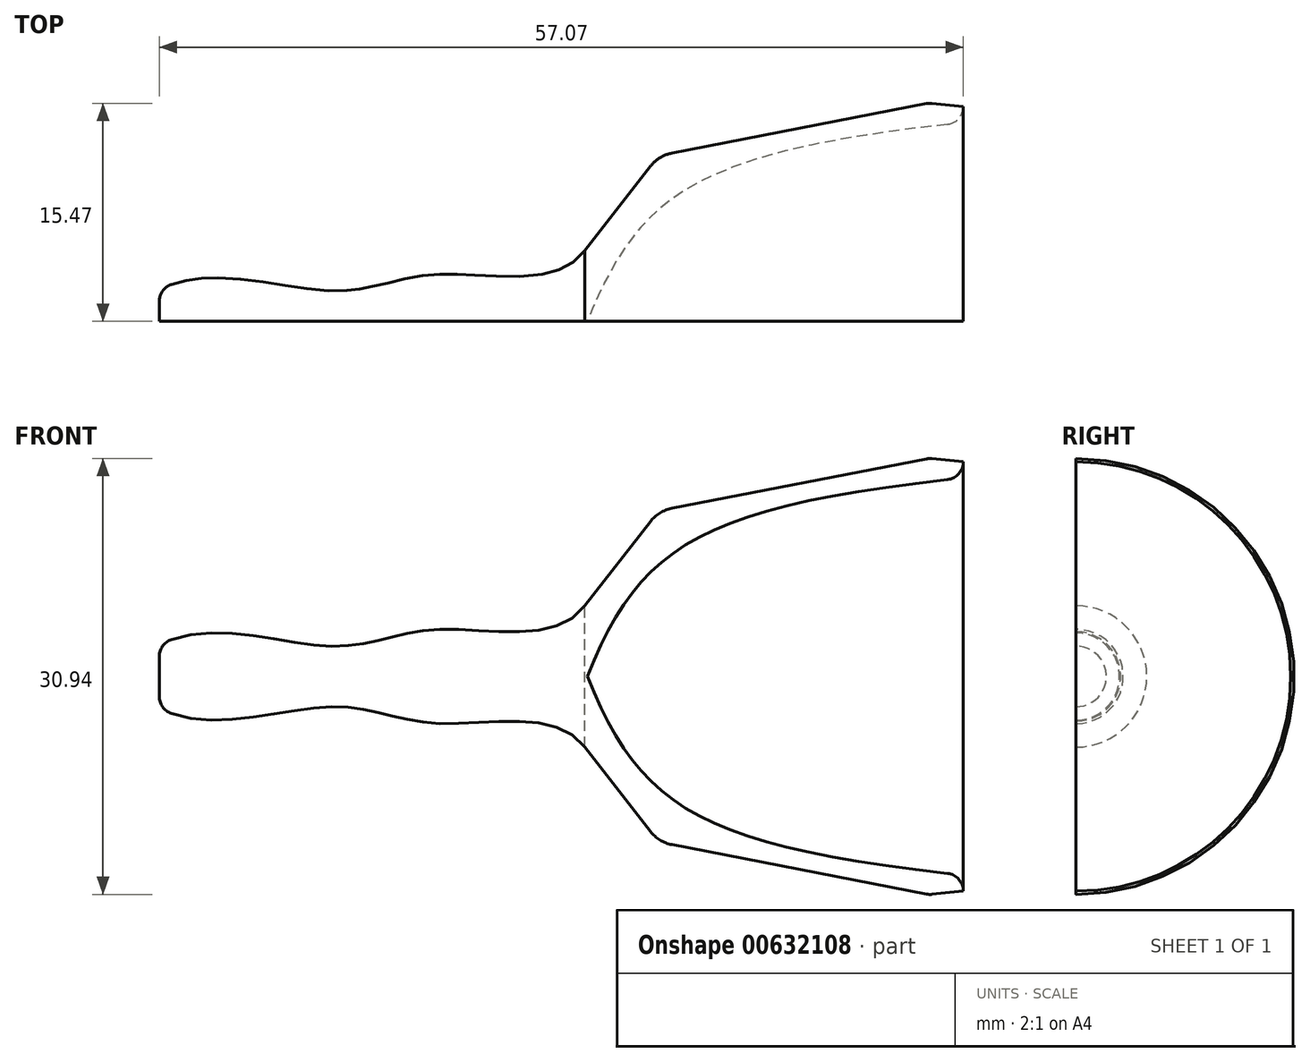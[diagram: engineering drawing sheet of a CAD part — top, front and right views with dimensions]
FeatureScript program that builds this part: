
annotation { "Feature Type Name" : "Feature", "Feature Type Description" : "" }
export const myFeature = defineFeature(function(context is Context, id is Id, definition is map)
    precondition{}
    {
        {
            var Q0;
            Q0=qCreatedBy(makeId("Front.planeOp"),FACE);
            var sketch = newSketch(context, id + "F0", { "sketchPlane" : qUnion([Q0])});
            skLineSegment(sketch, "E0", {"start": v(0, 0) * mm, "end": v(0, 1.42) * mm});
            skLineSegment(sketch, "E1", {"start": v(57.07, 15.24) * mm, "end": v(57.07, 13.75) * mm});
            skLineSegment(sketch, "E2", {"start": v(30.37, 0) * mm, "end": v(0, 0) * mm});
            skFitSpline(sketch, "E3", {"points": [v(30.37, 0) * mm, v(57.07, 14.1) * mm], "startDerivative": vector(11.3, 27.72) * mm, "endDerivative": vector(56.6, 6.15) * mm});
            skArc(sketch, "E4.filletArc", {"start": v(55.94, 13.98) * mm, "mid": v(56.75, 14.4) * mm, "end": v(57.07, 15.24) * mm});
            skFitSpline(sketch, "E5", {"points": [v(0, 2.26) * mm, v(12.34, 2.15) * mm, v(19.86, 3.34) * mm, v(30.2, 5.02) * mm], "startDerivative": vector(30.3, 15.5) * mm, "endDerivative": vector(18.37, 24.65) * mm});
            skLineSegment(sketch, "E6", {"start": v(36.38, 11.94) * mm, "end": v(54.46, 15.45) * mm});
            skLineSegment(sketch, "E7", {"start": v(54.83, 15.47) * mm, "end": v(57.07, 15.24) * mm});
            skArc(sketch, "E8.filletArc", {"start": v(0.85, 2.62) * mm, "mid": v(0.23, 2.16) * mm, "end": v(0, 1.42) * mm});
            skLineSegment(sketch, "E9", {"start": v(34.86, 11) * mm, "end": v(30.2, 5.02) * mm});
            skPoint(sketch, "E10.visualSharp", {"position": v(35.44, 11.76) * mm});
            skArc(sketch, "E10.filletArc", {"start": v(36.38, 11.94) * mm, "mid": v(35.53, 11.6) * mm, "end": v(34.86, 11) * mm});
            skPoint(sketch, "E11.visualSharp", {"position": v(54.65, 15.48) * mm});
            skArc(sketch, "E11.filletArc", {"start": v(54.83, 15.47) * mm, "mid": v(54.65, 15.47) * mm, "end": v(54.46, 15.45) * mm});
            skSolve(sketch);
        }
        {
            var Q0;
            Q0=makeQuery(id+"F0.imprint","IMPRINT",FACE,{"disambiguationData":[TD([[makeQuery(id+"F0.imprint","IMPRINT",EDGE,{"derivedFrom":sQuery(id+"F0.wireOp",EDGE,"E0")}),-1.0]])]});
            var Q1;
            Q1=sQuery(id+"F0.wireOp",EDGE,"E2");
            revolve(context, id + "F1", {"surfaceOperationType" : NewSurfaceOperationType.NEW, "entities" : qUnion([Q0]), "axis" : qUnion([Q1]), "revolveType" : RevolveType.ONE_DIRECTION, "angle" : 180 * degree});
        }
    });
